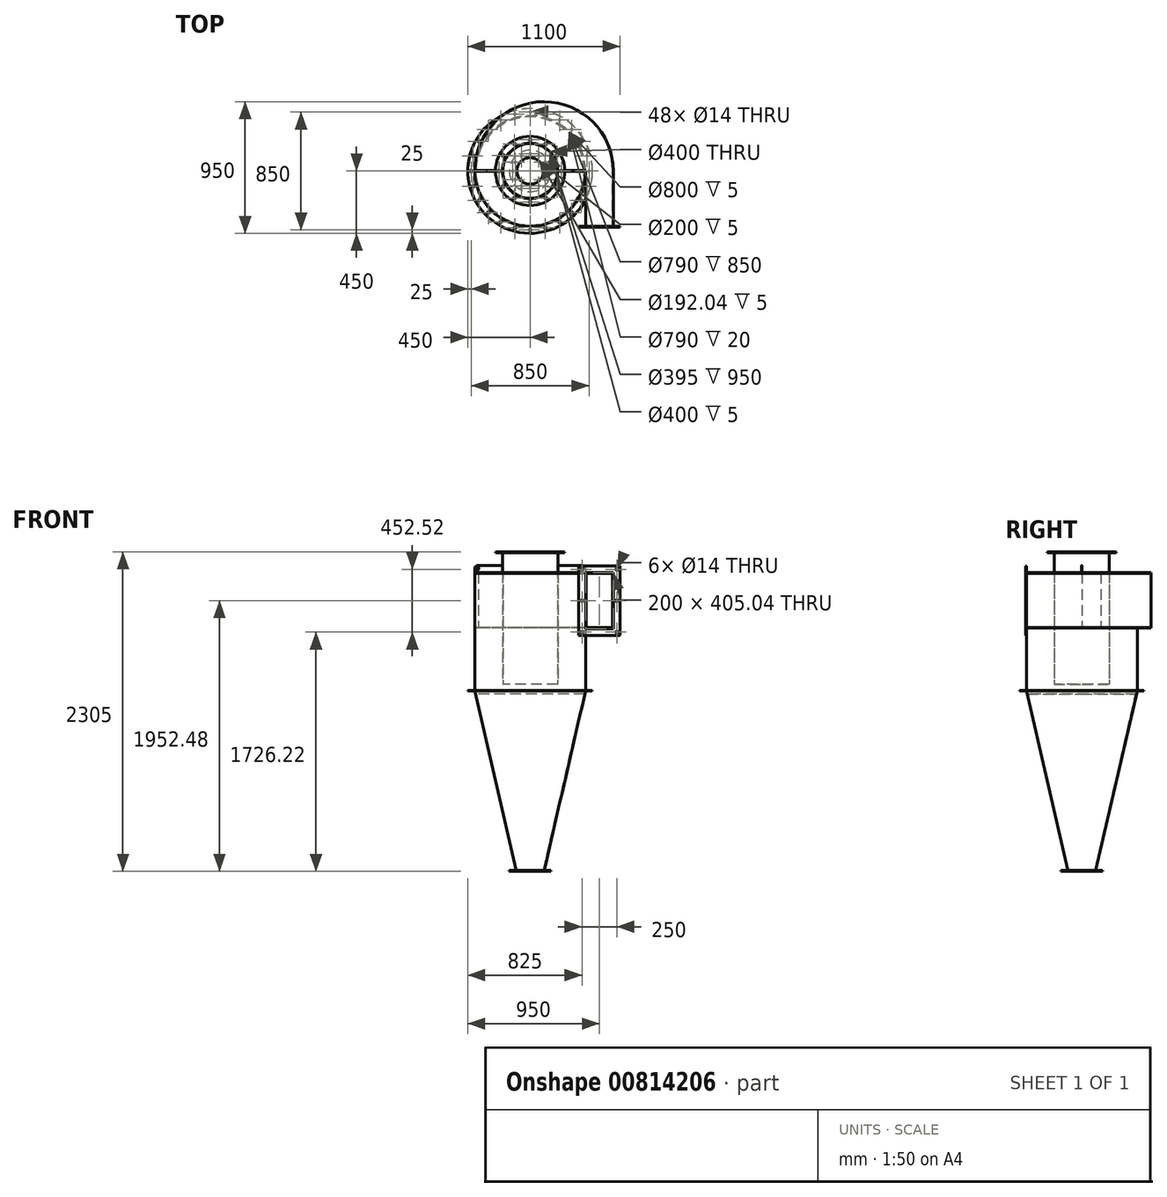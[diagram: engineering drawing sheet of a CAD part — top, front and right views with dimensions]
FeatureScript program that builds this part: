
annotation { "Feature Type Name" : "Feature", "Feature Type Description" : "" }
export const myFeature = defineFeature(function(context is Context, id is Id, definition is map)
    precondition{}
    {
        {
            var Q0;
            Q0=qCreatedBy(makeId("Top.planeOp"),FACE);
            var sketch = newSketch(context, id + "F0", { "sketchPlane" : qUnion([Q0])});
            skCircle(sketch, "E0", {"center": v(0, 0) * mm, "radius": 150 * mm});
            skCircle(sketch, "E1", {"center": v(0, 0) * mm, "radius": 100 * mm});
            skLineSegment(sketch, "E2", {"start": v(0, 100) * mm, "end": v(0, 150) * mm, "construction": true});
            skPoint(sketch, "E3", {"position": v(0, 150) * mm});
            skPoint(sketch, "E4", {"position": v(0, 100) * mm});
            skCircle(sketch, "E5", {"center": v(0, 125) * mm, "radius": 7 * mm});
            skCircle(sketch, "E6.1.0", {"center": v(-62.5, 108.25) * mm, "radius": 7 * mm});
            skCircle(sketch, "E6.2.0", {"center": v(-108.25, 62.5) * mm, "radius": 7 * mm});
            skCircle(sketch, "E7.1.3.0", {"center": v(-125, 0) * mm, "radius": 7 * mm});
            skCircle(sketch, "E7.1.4.0", {"center": v(-108.25, -62.5) * mm, "radius": 7 * mm});
            skCircle(sketch, "E7.1.5.0", {"center": v(-62.5, -108.25) * mm, "radius": 7 * mm});
            skCircle(sketch, "E7.1.6.0", {"center": v(0, -125) * mm, "radius": 7 * mm});
            skCircle(sketch, "E7.1.7.0", {"center": v(62.5, -108.25) * mm, "radius": 7 * mm});
            skCircle(sketch, "E7.1.8.0", {"center": v(108.25, -62.5) * mm, "radius": 7 * mm});
            skCircle(sketch, "E7.1.9.0", {"center": v(125, 0) * mm, "radius": 7 * mm});
            skCircle(sketch, "E7.1.10.0", {"center": v(108.25, 62.5) * mm, "radius": 7 * mm});
            skCircle(sketch, "E7.1.11.0", {"center": v(62.5, 108.25) * mm, "radius": 7 * mm});
            skSolve(sketch);
        }
        {
            var Q0;
            Q0=makeQuery(id+"F0.imprint","IMPRINT",FACE,{"disambiguationData":[TD([[makeQuery(id+"F0.imprint","IMPRINT",EDGE,{"derivedFrom":sQuery(id+"F0.wireOp",EDGE,"E0")}),1.0]])]});
            extrude(context, id + "F1", {"entities" : qUnion([Q0]), "depth" : 5 * mm, "offsetDistance" : 25 * mm});
        }
        {
            var Q0;
            Q0=makeQuery(id+"F0.imprint","IMPRINT",FACE,{"disambiguationData":[TD([[makeQuery(id+"F0.imprint","IMPRINT",EDGE,{"derivedFrom":sQuery(id+"F0.wireOp",EDGE,"E0")}),1.0]])]});
            cPlane(context, id + "F2", {"entities" : qUnion([Q0]), "cplaneType" : CPlaneType.OFFSET, "offset" : 1300 * mm, "width" : 150 * mm, "height" : 150 * mm});
        }
        {
            var Q0;
            Q0=qCreatedBy(id+"F2.planeOp",FACE);
            var sketch = newSketch(context, id + "F3", { "sketchPlane" : qUnion([Q0])});
            skCircle(sketch, "E8", {"center": v(0, 0) * mm, "radius": 400 * mm});
            skCircle(sketch, "E9", {"center": v(0, 0) * mm, "radius": 450 * mm});
            skLineSegment(sketch, "E10", {"start": v(0, 400) * mm, "end": v(0, 450) * mm, "construction": true});
            skPoint(sketch, "E11", {"position": v(0, 425) * mm});
            skCircle(sketch, "E12", {"center": v(0, 425) * mm, "radius": 7 * mm});
            skCircle(sketch, "E13.1.0", {"center": v(-110, 410.52) * mm, "radius": 7 * mm});
            skCircle(sketch, "E13.2.0", {"center": v(-212.5, 368.06) * mm, "radius": 7 * mm});
            skCircle(sketch, "E13.3.0", {"center": v(-300.52, 300.52) * mm, "radius": 7 * mm});
            skCircle(sketch, "E13.4.0", {"center": v(-368.06, 212.5) * mm, "radius": 7 * mm});
            skCircle(sketch, "E13.5.0", {"center": v(-410.52, 110) * mm, "radius": 7 * mm});
            skCircle(sketch, "E13.6.0", {"center": v(-425, 0) * mm, "radius": 7 * mm});
            skCircle(sketch, "E13.7.0", {"center": v(-410.52, -110) * mm, "radius": 7 * mm});
            skCircle(sketch, "E13.8.0", {"center": v(-368.06, -212.5) * mm, "radius": 7 * mm});
            skCircle(sketch, "E13.9.0", {"center": v(-300.52, -300.52) * mm, "radius": 7 * mm});
            skCircle(sketch, "E13.10.0", {"center": v(-212.5, -368.06) * mm, "radius": 7 * mm});
            skCircle(sketch, "E13.11.0", {"center": v(-110, -410.52) * mm, "radius": 7 * mm});
            skCircle(sketch, "E13.12.0", {"center": v(0, -425) * mm, "radius": 7 * mm});
            skCircle(sketch, "E13.13.0", {"center": v(110, -410.52) * mm, "radius": 7 * mm});
            skCircle(sketch, "E13.14.0", {"center": v(212.5, -368.06) * mm, "radius": 7 * mm});
            skCircle(sketch, "E13.15.0", {"center": v(300.52, -300.52) * mm, "radius": 7 * mm});
            skCircle(sketch, "E13.16.0", {"center": v(368.06, -212.5) * mm, "radius": 7 * mm});
            skCircle(sketch, "E13.17.0", {"center": v(410.52, -110) * mm, "radius": 7 * mm});
            skCircle(sketch, "E13.18.0", {"center": v(425, 0) * mm, "radius": 7 * mm});
            skCircle(sketch, "E13.19.0", {"center": v(410.52, 110) * mm, "radius": 7 * mm});
            skCircle(sketch, "E13.20.0", {"center": v(368.06, 212.5) * mm, "radius": 7 * mm});
            skCircle(sketch, "E13.21.0", {"center": v(300.52, 300.52) * mm, "radius": 7 * mm});
            skCircle(sketch, "E13.22.0", {"center": v(212.5, 368.06) * mm, "radius": 7 * mm});
            skCircle(sketch, "E13.23.0", {"center": v(110, 410.52) * mm, "radius": 7 * mm});
            skSolve(sketch);
        }
        {
            var Q0;
            Q0=makeQuery(id+"F3.imprint","IMPRINT",FACE,{"disambiguationData":[TD([[makeQuery(id+"F3.imprint","IMPRINT",EDGE,{"derivedFrom":sQuery(id+"F3.wireOp",EDGE,"E8")}),-1.0]])]});
            extrude(context, id + "F4", {"entities" : qUnion([Q0]), "depth" : 5 * mm, "offsetDistance" : 25 * mm});
        }
        {
            var Q0;
            Q0=qCreatedBy(makeId("Top.planeOp"),FACE);
            var sketch = newSketch(context, id + "F5", { "sketchPlane" : qUnion([Q0])});
            skCircle(sketch, "E14", {"center": v(0, 0) * mm, "radius": 100 * mm});
            skSolve(sketch);
        }
        {
            var Q0;
            Q0=qCreatedBy(id+"F2.planeOp",FACE);
            var sketch = newSketch(context, id + "F6", { "sketchPlane" : qUnion([Q0])});
            skCircle(sketch, "E15", {"center": v(0, 0) * mm, "radius": 400 * mm});
            skSolve(sketch);
        }
        {
            var Q0;
            Q0=makeQuery(id+"F6.imprint","IMPRINT",FACE,{"disambiguationData":[TD([[makeQuery(id+"F6.imprint","IMPRINT",EDGE,{"derivedFrom":sQuery(id+"F6.wireOp",EDGE,"E15")}),1.0]])]});
            var Q1;
            Q1 = qSketchRegion(id + "F5", true);
            loft(context, id + "F7", {"sheetProfilesArray" : [{ "sheetProfileEntities" : qUnion([Q0]) }, { "sheetProfileEntities" : qUnion([Q1]) }]});
        }
        {
            var Q0;
            Q0=makeQuery(id+"F7.opLoft","CAP_FACE",FACE,{"disambiguationData":[OSD([makeQuery(id+"F6.imprint","IMPRINT",FACE,{"disambiguationData":[TD([[makeQuery(id+"F6.imprint","IMPRINT",EDGE,{"derivedFrom":sQuery(id+"F6.wireOp",EDGE,"E15")}),1.0]])]})])],"isStart":true});
            shell(context, id + "F8", {"entities" : qUnion([Q0]), "thickness" : 5 * mm});
        }
        {
            var Q0;
            Q0=makeQuery(id+"F8.opShell","OFFSET_FACE",FACE,{"disambiguationData":[OSD([makeQuery(id+"F5.imprint","IMPRINT",FACE,{"disambiguationData":[TD([[makeQuery(id+"F5.imprint","IMPRINT",EDGE,{"derivedFrom":sQuery(id+"F5.wireOp",EDGE,"E14")}),1.0]])]})])]});
            extrude(context, id + "F9", {"entities" : qUnion([Q0]), "operationType" : NewBodyOperationType.REMOVE, "oppositeDirection" : true, "depth" : 25 * mm, "offsetDistance" : 25 * mm});
        }
        {
            var Q0;
            Q0 = qSketchRegion(id + "F6", true);
            extrude(context, id + "F10", {"entities" : qUnion([Q0]), "depth" : 850 * mm, "offsetDistance" : 25 * mm});
        }
        {
            var Q0;
            Q0=makeQuery(id+"F10.opExtrude","CAP_FACE",FACE,{"disambiguationData":[OSD([sQuery(id+"F6.wireOp",EDGE,"E15")])],"isStart":false});
            shell(context, id + "F11", {"entities" : qUnion([Q0]), "thickness" : 5 * mm});
        }
        {
            var Q0;
            {var subQ0=sQuery(id+"F6.wireOp",EDGE,"E15");Q0=makeQuery(id+"F11.opShell","OFFSET_FACE",FACE,{"disambiguationData":[OSD([subQ0]),TDD([makeQuery(id+"F10.opExtrude","CAP_FACE",FACE,{"disambiguationData":[OSD([subQ0])],"isStart":true})])]});}
            extrude(context, id + "F12", {"entities" : qUnion([Q0]), "operationType" : NewBodyOperationType.REMOVE, "oppositeDirection" : true, "depth" : 25 * mm, "offsetDistance" : 25 * mm});
        }
        {
            var Q0;
            Q0=makeQuery(id+"F4.opExtrude","CAP_FACE",FACE,{"disambiguationData":[OSD([sQuery(id+"F3.wireOp",EDGE,"E8"),sQuery(id+"F3.wireOp",EDGE,"E9"),sQuery(id+"F3.wireOp",EDGE,"E12"),sQuery(id+"F3.wireOp",EDGE,"E13.1.0"),sQuery(id+"F3.wireOp",EDGE,"E13.2.0"),sQuery(id+"F3.wireOp",EDGE,"E13.3.0"),sQuery(id+"F3.wireOp",EDGE,"E13.4.0"),sQuery(id+"F3.wireOp",EDGE,"E13.5.0"),sQuery(id+"F3.wireOp",EDGE,"E13.6.0"),sQuery(id+"F3.wireOp",EDGE,"E13.7.0"),sQuery(id+"F3.wireOp",EDGE,"E13.8.0"),sQuery(id+"F3.wireOp",EDGE,"E13.9.0"),sQuery(id+"F3.wireOp",EDGE,"E13.10.0"),sQuery(id+"F3.wireOp",EDGE,"E13.11.0"),sQuery(id+"F3.wireOp",EDGE,"E13.12.0"),sQuery(id+"F3.wireOp",EDGE,"E13.13.0"),sQuery(id+"F3.wireOp",EDGE,"E13.14.0"),sQuery(id+"F3.wireOp",EDGE,"E13.15.0"),sQuery(id+"F3.wireOp",EDGE,"E13.16.0"),sQuery(id+"F3.wireOp",EDGE,"E13.17.0"),sQuery(id+"F3.wireOp",EDGE,"E13.18.0"),sQuery(id+"F3.wireOp",EDGE,"E13.19.0"),sQuery(id+"F3.wireOp",EDGE,"E13.20.0"),sQuery(id+"F3.wireOp",EDGE,"E13.21.0"),sQuery(id+"F3.wireOp",EDGE,"E13.22.0"),sQuery(id+"F3.wireOp",EDGE,"E13.23.0")])],"isStart":false});
            cPlane(context, id + "F13", {"entities" : qUnion([Q0]), "cplaneType" : CPlaneType.OFFSET, "offset" : 450 * mm, "width" : 150 * mm, "height" : 150 * mm});
        }
        {
            var Q0;
            Q0=qCreatedBy(id+"F13.planeOp",FACE);
            var sketch = newSketch(context, id + "F14", { "sketchPlane" : qUnion([Q0])});
            skLineSegment(sketch, "E16.bottom", {"start": v(-526, 0) * mm, "end": v(526, 0) * mm});
            skLineSegment(sketch, "E16.top", {"start": v(-526, 503) * mm, "end": v(526, 503) * mm});
            skLineSegment(sketch, "E16.left", {"start": v(-526, 0) * mm, "end": v(-526, 503) * mm});
            skLineSegment(sketch, "E16.right", {"start": v(526, 0) * mm, "end": v(526, 503) * mm});
            skSolve(sketch);
        }
        {
            var Q0;
            Q0=makeQuery(id+"F14.imprint","IMPRINT",FACE,{"disambiguationData":[TD([[makeQuery(id+"F14.imprint","IMPRINT",EDGE,{"derivedFrom":sQuery(id+"F14.wireOp",EDGE,"E16.bottom")}),1.0]])]});
            extrude(context, id + "F15", {"entities" : qUnion([Q0]), "operationType" : NewBodyOperationType.REMOVE, "depth" : 400 * mm, "offsetDistance" : 25 * mm});
        }
        {
            var Q0;
            Q0=qCreatedBy(id+"F13.planeOp",FACE);
            var sketch = newSketch(context, id + "F16", { "sketchPlane" : qUnion([Q0])});
            skLineSegment(sketch, "E17", {"start": v(-417.92, 0) * mm, "end": v(-417.92, 0) * mm});
            skLineSegment(sketch, "E18", {"start": v(382.08, 0) * mm, "end": v(400, 0) * mm, "construction": true});
            skLineSegment(sketch, "E19", {"start": v(-417.92, 0) * mm, "end": v(382.08, 0) * mm, "construction": true});
            skArc(sketch, "E20", {"start": v(400, 0) * mm, "mid": v(0, 400) * mm, "end": v(-400, 0) * mm});
            skLineSegment(sketch, "E21", {"start": v(0, 0) * mm, "end": v(100, 0) * mm, "construction": true});
            skArc(sketch, "E22", {"start": v(-400, 0) * mm, "mid": v(100, 500) * mm, "end": v(600, 0) * mm});
            skLineSegment(sketch, "E23", {"start": v(400, 0) * mm, "end": v(400, -400) * mm});
            skLineSegment(sketch, "E24", {"start": v(400, -400) * mm, "end": v(600, -400) * mm});
            skLineSegment(sketch, "E25", {"start": v(600, -400) * mm, "end": v(600, 0) * mm});
            skSolve(sketch);
        }
        {
            var Q0;
            Q0=makeQuery(id+"F16.imprint","IMPRINT",FACE,{"disambiguationData":[TD([[makeQuery(id+"F16.imprint","IMPRINT",EDGE,{"derivedFrom":sQuery(id+"F16.wireOp",EDGE,"E20")}),-1.0]])]});
            extrude(context, id + "F17", {"entities" : qUnion([Q0]), "depth" : 5 * mm, "offsetDistance" : 25 * mm});
        }
        {
            var Q0;
            Q0=makeQuery(id+"F17.opExtrude","CAP_FACE",FACE,{"disambiguationData":[OSD([sQuery(id+"F16.wireOp",EDGE,"E20"),sQuery(id+"F16.wireOp",EDGE,"E22"),sQuery(id+"F16.wireOp",EDGE,"E23"),sQuery(id+"F16.wireOp",EDGE,"E24"),sQuery(id+"F16.wireOp",EDGE,"E25")])],"isStart":false});
            var sketch = newSketch(context, id + "F18", { "sketchPlane" : qUnion([Q0])});
            skLineSegment(sketch, "E26.bottom", {"start": v(400, -400) * mm, "end": v(405, -400) * mm});
            skLineSegment(sketch, "E26.top", {"start": v(400, 0) * mm, "end": v(405, 0) * mm});
            skLineSegment(sketch, "E26.left", {"start": v(400, -400) * mm, "end": v(400, 0) * mm});
            skLineSegment(sketch, "E26.right", {"start": v(405, -400) * mm, "end": v(405, 0) * mm});
            skSolve(sketch);
        }
        {
            var Q0;
            Q0=makeQuery(id+"F18.imprint","IMPRINT",FACE,{"disambiguationData":[TD([[makeQuery(id+"F18.imprint","IMPRINT",EDGE,{"derivedFrom":sQuery(id+"F18.wireOp",EDGE,"E26.bottom")}),1.0]])]});
            extrude(context, id + "F19", {"entities" : qUnion([Q0]), "operationType" : NewBodyOperationType.ADD, "depth" : 390 * mm, "offsetDistance" : 25 * mm});
        }
        {
            var Q0;
            Q0=qCreatedBy(id+"F13.planeOp",FACE);
            cPlane(context, id + "F20", {"entities" : qUnion([Q0]), "cplaneType" : CPlaneType.OFFSET, "offset" : 395 * mm, "width" : 150 * mm, "height" : 150 * mm});
        }
        {
            var Q0;
            Q0=qCreatedBy(id+"F20.planeOp",FACE);
            var sketch = newSketch(context, id + "F21", { "sketchPlane" : qUnion([Q0])});
            skCircle(sketch, "E27", {"center": v(0, 0) * mm, "radius": 200 * mm});
            skLineSegment(sketch, "E28", {"start": v(-452.32, 0) * mm, "end": v(652.32, 0) * mm, "construction": true});
            skArc(sketch, "E29", {"start": v(-400, 0) * mm, "mid": v(0, -400) * mm, "end": v(400, 0) * mm});
            skPoint(sketch, "E30", {"position": v(100, 0) * mm});
            skArc(sketch, "E31", {"start": v(-400, 0) * mm, "mid": v(100, 500) * mm, "end": v(600, 0) * mm});
            skLineSegment(sketch, "E32", {"start": v(600, 0) * mm, "end": v(600, -400) * mm});
            skLineSegment(sketch, "E33", {"start": v(600, -400) * mm, "end": v(400, -400) * mm});
            skLineSegment(sketch, "E34", {"start": v(400, -400) * mm, "end": v(400, 0) * mm});
            skSolve(sketch);
        }
        {
            var Q0;
            Q0=makeQuery(id+"F21.imprint","IMPRINT",FACE,{"disambiguationData":[TD([[makeQuery(id+"F21.imprint","IMPRINT",EDGE,{"derivedFrom":sQuery(id+"F21.wireOp",EDGE,"E27")}),-1.0]])]});
            extrude(context, id + "F22", {"entities" : qUnion([Q0]), "depth" : 5 * mm, "offsetDistance" : 25 * mm});
        }
        {
            var Q0;
            Q0=qCreatedBy(id+"F20.planeOp",FACE);
            var sketch = newSketch(context, id + "F23", { "sketchPlane" : qUnion([Q0])});
            skCircle(sketch, "E35", {"center": v(0, 0) * mm, "radius": 199.5 * mm});
            skCircle(sketch, "E36.0", {"center": v(0, 0) * mm, "radius": 197.5 * mm});
            skSolve(sketch);
        }
        {
            var Q0;
            Q0=makeQuery(id+"F23.imprint","IMPRINT",FACE,{"disambiguationData":[TD([[makeQuery(id+"F23.imprint","IMPRINT",EDGE,{"derivedFrom":sQuery(id+"F23.wireOp",EDGE,"E35")}),1.0]])]});
            extrude(context, id + "F24", {"entities" : qUnion([Q0]), "depth" : 950 * mm, "offsetDistance" : 25 * mm});
        }
        {
            var Q0;
            Q0=qCreatedBy(makeId("Front.planeOp"),FACE);
            var sketch = newSketch(context, id + "F25", { "sketchPlane" : qUnion([Q0])});
            skLineSegment(sketch, "E37", {"start": v(0, 0) * mm, "end": v(0, 3754) * mm, "construction": true});
            skSolve(sketch);
        }
        {
            var Q0;
            Q0=makeQuery(id+"F24.opExtrude","SWEPT_BODY",BODY,{"disambiguationData":[OSD([sQuery(id+"F23.wireOp",EDGE,"E35"),sQuery(id+"F23.wireOp",EDGE,"E36.0")])]});
            var Q1;
            Q1=sQuery(id+"F25.wireOp",EDGE,"E37");
            transform(context, id + "F26", {"entities" : qUnion([Q0]), "transformType" : TransformType.TRANSLATION_DISTANCE, "transformDirection" : qUnion([Q1]), "distance" : 800 * mm, "oppositeDirection" : true, "makeCopy" : false});
        }
        {
            var Q0;
            Q0=makeQuery(id+"F22.opExtrude","SWEPT_FACE",FACE,{"disambiguationData":[OSD([sQuery(id+"F21.wireOp",EDGE,"E33")])]});
            var sketch = newSketch(context, id + "F27", { "sketchPlane" : qUnion([Q0])});
            skPoint(sketch, "E38.0", {"position": v(400, 2155) * mm});
            skPoint(sketch, "E38.1", {"position": v(600, 2155) * mm});
            skLineSegment(sketch, "E39.left", {"start": v(400, 2150) * mm, "end": v(400, 2155) * mm});
            skLineSegment(sketch, "E39.right", {"start": v(600, 2155) * mm, "end": v(600, 2155) * mm});
            skLineSegment(sketch, "E40.left", {"start": v(400, 1755) * mm, "end": v(400, 1755) * mm});
            skLineSegment(sketch, "E40.right", {"start": v(600, 1749.96) * mm, "end": v(600, 1755) * mm});
            skLineSegment(sketch, "E41.left", {"start": v(400, 2155) * mm, "end": v(400, 2155) * mm});
            skLineSegment(sketch, "E42.bottom", {"start": v(400, 2155) * mm, "end": v(600, 2155) * mm});
            skLineSegment(sketch, "E42.top", {"start": v(400, 1749.96) * mm, "end": v(600, 1749.96) * mm});
            skLineSegment(sketch, "E42.left", {"start": v(400, 2155) * mm, "end": v(400, 1749.96) * mm});
            skLineSegment(sketch, "E42.right", {"start": v(600, 2155) * mm, "end": v(600, 1749.96) * mm});
            skLineSegment(sketch, "E43.bottom", {"start": v(350, 2202.48) * mm, "end": v(650, 2202.48) * mm});
            skLineSegment(sketch, "E43.top", {"start": v(350, 1702.48) * mm, "end": v(650, 1702.48) * mm});
            skLineSegment(sketch, "E43.left", {"start": v(350, 2202.48) * mm, "end": v(350, 1702.48) * mm});
            skLineSegment(sketch, "E43.right", {"start": v(650, 2202.48) * mm, "end": v(650, 1702.48) * mm});
            skLineSegment(sketch, "E44", {"start": v(350, 2202.48) * mm, "end": v(400, 2155) * mm, "construction": true});
            skLineSegment(sketch, "E45", {"start": v(600, 1749.96) * mm, "end": v(650, 1702.48) * mm, "construction": true});
            skLineSegment(sketch, "E46", {"start": v(600, 2155) * mm, "end": v(650, 2202.48) * mm, "construction": true});
            skLineSegment(sketch, "E47.bottom", {"start": v(375, 2178.74) * mm, "end": v(625, 2178.74) * mm, "construction": true});
            skLineSegment(sketch, "E47.top", {"start": v(375, 1726.22) * mm, "end": v(625, 1726.22) * mm, "construction": true});
            skLineSegment(sketch, "E47.left", {"start": v(375, 2178.74) * mm, "end": v(375, 1726.22) * mm, "construction": true});
            skLineSegment(sketch, "E47.right", {"start": v(625, 2178.74) * mm, "end": v(625, 1726.22) * mm, "construction": true});
            skCircle(sketch, "E48", {"center": v(375, 2178.74) * mm, "radius": 7 * mm});
            skCircle(sketch, "E49", {"center": v(625, 2178.74) * mm, "radius": 7 * mm});
            skCircle(sketch, "E50", {"center": v(375, 1726.22) * mm, "radius": 7 * mm});
            skCircle(sketch, "E51", {"center": v(625, 1726.22) * mm, "radius": 7 * mm});
            skCircle(sketch, "E52", {"center": v(375, 1952.48) * mm, "radius": 7 * mm});
            skCircle(sketch, "E53", {"center": v(625, 1952.48) * mm, "radius": 7 * mm});
            skSolve(sketch);
        }
        {
            var Q0;
            {var subQ5=sQuery(id+"F27.wireOp",EDGE,"E42.bottom");Q0=makeQuery(id+"F27.imprint","IMPRINT",FACE,{"disambiguationData":[TD([[makeQuery(id+"F27.imprint","IMPRINT",EDGE,{"derivedFrom":subQ5}),-1.0]])]});}
            extrude(context, id + "F28", {"entities" : qUnion([Q0]), "depth" : 5 * mm, "offsetDistance" : 25 * mm});
        }
        {
            var Q0;
            Q0=qCreatedBy(makeId("Front.planeOp"),FACE);
            var sketch = newSketch(context, id + "F29", { "sketchPlane" : qUnion([Q0])});
            skPoint(sketch, "E54.0", {"position": v(-400, 2155) * mm});
            skLineSegment(sketch, "E55.bottom", {"start": v(-400, 2155) * mm, "end": v(-200, 2155) * mm});
            skLineSegment(sketch, "E55.top", {"start": v(-380, 2205) * mm, "end": v(-200, 2205) * mm});
            skLineSegment(sketch, "E55.left", {"start": v(-400, 2155) * mm, "end": v(-400, 2185) * mm});
            skLineSegment(sketch, "E55.right", {"start": v(-200, 2155) * mm, "end": v(-200, 2205) * mm});
            skPoint(sketch, "E56.visualSharp", {"position": v(-400, 2205) * mm});
            skArc(sketch, "E56.filletArc", {"start": v(-380, 2205) * mm, "mid": v(-394.14, 2199.14) * mm, "end": v(-400, 2185) * mm});
            skCircle(sketch, "E57", {"center": v(-380, 2185) * mm, "radius": 10 * mm});
            skLineSegment(sketch, "E58", {"start": v(0, 2122.95) * mm, "end": v(0, 2352.2) * mm, "construction": true});
            skArc(sketch, "E59.MirrorCS", {"start": v(380, 2205) * mm, "mid": v(394.14, 2199.14) * mm, "end": v(400, 2185) * mm});
            skLineSegment(sketch, "E60.MirrorCS", {"start": v(400, 2155) * mm, "end": v(400, 2185) * mm});
            skLineSegment(sketch, "E61.MirrorCS", {"start": v(200, 2155) * mm, "end": v(200, 2205) * mm});
            skCircle(sketch, "E62.MirrorC", {"center": v(380, 2185) * mm, "radius": 10 * mm});
            skLineSegment(sketch, "E63.MirrorCS", {"start": v(400, 2155) * mm, "end": v(200, 2155) * mm});
            skLineSegment(sketch, "E64.MirrorCS", {"start": v(380, 2205) * mm, "end": v(200, 2205) * mm});
            skPoint(sketch, "E65.MirrorP", {"position": v(400, 2155) * mm});
            skPoint(sketch, "E66.MirrorP", {"position": v(400, 2205) * mm});
            skSolve(sketch);
        }
        {
            var Q0;
            Q0=makeQuery(id+"F29.imprint","IMPRINT",FACE,{"disambiguationData":[TD([[makeQuery(id+"F29.imprint","IMPRINT",EDGE,{"derivedFrom":sQuery(id+"F29.wireOp",EDGE,"E55.bottom")}),1.0]])]});
            extrude(context, id + "F30", {"entities" : qUnion([Q0]), "endBound" : BoundingType.SYMMETRIC, "depth" : 5 * mm, "offsetDistance" : 25 * mm});
        }
        {
            var Q0;
            Q0=makeQuery(id+"F24.opExtrude","CAP_FACE",FACE,{"disambiguationData":[OSD([sQuery(id+"F23.wireOp",EDGE,"E35"),sQuery(id+"F23.wireOp",EDGE,"E36.0")])],"isStart":false});
            var sketch = newSketch(context, id + "F31", { "sketchPlane" : qUnion([Q0])});
            skCircle(sketch, "E67", {"center": v(0, 0) * mm, "radius": 200 * mm});
            skCircle(sketch, "E68.0", {"center": v(0, 0) * mm, "radius": 250 * mm});
            skLineSegment(sketch, "E69", {"start": v(0, 200) * mm, "end": v(0, 250) * mm, "construction": true});
            skCircle(sketch, "E70", {"center": v(0, 225) * mm, "radius": 7 * mm});
            skCircle(sketch, "E71.1.0", {"center": v(-112.5, 194.86) * mm, "radius": 7 * mm});
            skCircle(sketch, "E71.2.0", {"center": v(-194.86, 112.5) * mm, "radius": 7 * mm});
            skCircle(sketch, "E72.1.3.0", {"center": v(-225, 0) * mm, "radius": 7 * mm});
            skCircle(sketch, "E72.1.4.0", {"center": v(-194.86, -112.5) * mm, "radius": 7 * mm});
            skCircle(sketch, "E72.1.5.0", {"center": v(-112.5, -194.86) * mm, "radius": 7 * mm});
            skCircle(sketch, "E72.1.6.0", {"center": v(0, -225) * mm, "radius": 7 * mm});
            skCircle(sketch, "E72.1.7.0", {"center": v(112.5, -194.86) * mm, "radius": 7 * mm});
            skCircle(sketch, "E72.1.8.0", {"center": v(194.86, -112.5) * mm, "radius": 7 * mm});
            skCircle(sketch, "E72.1.9.0", {"center": v(225, 0) * mm, "radius": 7 * mm});
            skCircle(sketch, "E72.1.10.0", {"center": v(194.86, 112.5) * mm, "radius": 7 * mm});
            skCircle(sketch, "E72.1.11.0", {"center": v(112.5, 194.86) * mm, "radius": 7 * mm});
            skSolve(sketch);
        }
        {
            var Q0;
            Q0=makeQuery(id+"F31.imprint","IMPRINT",FACE,{"disambiguationData":[TD([[makeQuery(id+"F31.imprint","IMPRINT",EDGE,{"derivedFrom":sQuery(id+"F31.wireOp",EDGE,"E67")}),-1.0]])]});
            extrude(context, id + "F32", {"entities" : qUnion([Q0]), "depth" : 5 * mm, "offsetDistance" : 25 * mm});
        }
        {
            var Q0;
            Q0=makeQuery(id+"F17.opExtrude","CAP_FACE",FACE,{"disambiguationData":[OSD([sQuery(id+"F16.wireOp",EDGE,"E20"),sQuery(id+"F16.wireOp",EDGE,"E22"),sQuery(id+"F16.wireOp",EDGE,"E23"),sQuery(id+"F16.wireOp",EDGE,"E24"),sQuery(id+"F16.wireOp",EDGE,"E25")])],"isStart":false});
            var sketch = newSketch(context, id + "F33", { "sketchPlane" : qUnion([Q0])});
            skPoint(sketch, "E73", {"position": v(100, 0) * mm});
            skArc(sketch, "E74", {"start": v(-395, 0) * mm, "mid": v(100, 495) * mm, "end": v(595, 0) * mm});
            skArc(sketch, "E75.0", {"start": v(-390, 0) * mm, "mid": v(100, 490) * mm, "end": v(590, 0) * mm});
            skLineSegment(sketch, "E76", {"start": v(-395, 0) * mm, "end": v(-390, 0) * mm});
            skLineSegment(sketch, "E77", {"start": v(590, 0) * mm, "end": v(590, -400) * mm});
            skLineSegment(sketch, "E78", {"start": v(590, -400) * mm, "end": v(595, -400) * mm});
            skLineSegment(sketch, "E79", {"start": v(595, -400) * mm, "end": v(595, 0) * mm});
            skSolve(sketch);
        }
        {
            var Q0;
            {var subQ2=sQuery(id+"F33.wireOp",EDGE,"E79");Q0=makeQuery(id+"F33.imprint","IMPRINT",FACE,{"disambiguationData":[TD([[makeQuery(id+"F33.imprint","IMPRINT",EDGE,{"derivedFrom":subQ2}),-1.0]])]});}
            extrude(context, id + "F34", {"entities" : qUnion([Q0]), "depth" : 390 * mm, "offsetDistance" : 25 * mm});
        }
        {
            var Q0;
            Q0=makeQuery(id+"F30.opExtrude","SWEPT_BODY",BODY,{"disambiguationData":[OSD([sQuery(id+"F29.wireOp",EDGE,"E55.bottom"),sQuery(id+"F29.wireOp",EDGE,"E55.top"),sQuery(id+"F29.wireOp",EDGE,"E55.left"),sQuery(id+"F29.wireOp",EDGE,"E55.right"),sQuery(id+"F29.wireOp",EDGE,"E56.filletArc"),sQuery(id+"F29.wireOp",EDGE,"E57")])]});
            var Q1;
            Q1=qCreatedBy(makeId("Right.planeOp"),FACE);
            mirror(context, id + "F35", {"entities" : qUnion([Q0]), "mirrorPlane" : qUnion([Q1])});
        }
    });
